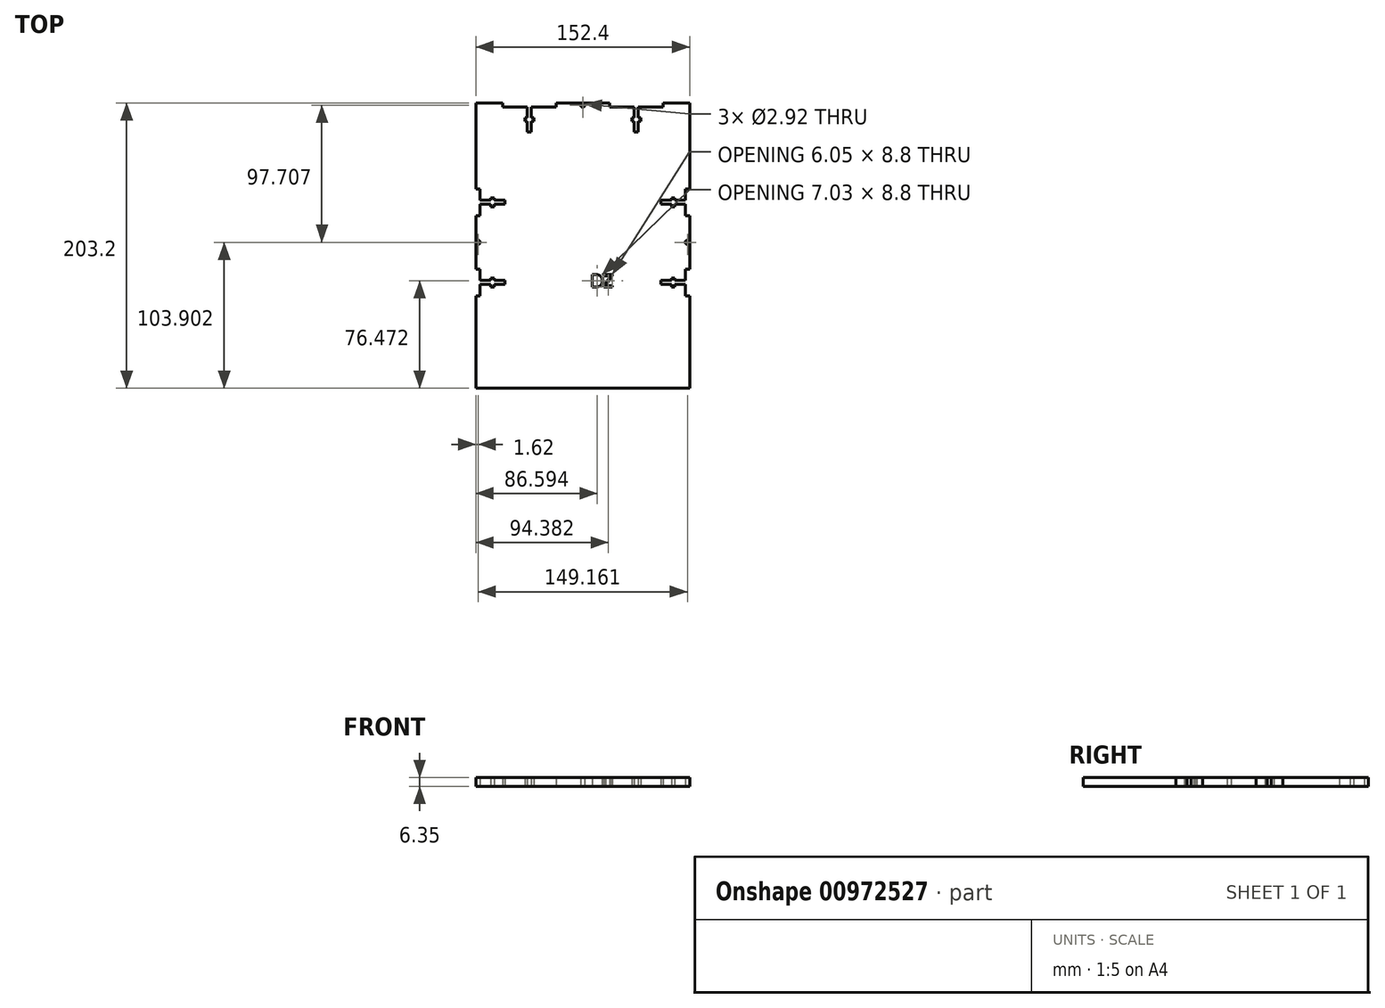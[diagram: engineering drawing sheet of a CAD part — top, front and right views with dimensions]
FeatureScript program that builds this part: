
annotation { "Feature Type Name" : "Feature", "Feature Type Description" : "" }
export const myFeature = defineFeature(function(context is Context, id is Id, definition is map)
    precondition{}
    {
        {
            var Q0;
            Q0=qCreatedBy(makeId("Top.planeOp"),FACE);
            var sketch = newSketch(context, id + "F0", { "sketchPlane" : qUnion([Q0])});
            skLineSegment(sketch, "E0.bottom", {"start": v(-76.2, 101.6) * mm, "end": v(-57.15, 101.6) * mm});
            skLineSegment(sketch, "E0.top", {"start": v(-76.2, -101.6) * mm, "end": v(76.2, -101.6) * mm});
            skLineSegment(sketch, "E0.left", {"start": v(-76.2, 101.6) * mm, "end": v(-76.2, 40.4) * mm});
            skLineSegment(sketch, "E0.right", {"start": v(76.2, 101.6) * mm, "end": v(76.2, 40.4) * mm});
            skLineSegment(sketch, "E1", {"start": v(0, 13.36) * mm, "end": v(-76.2, 13.36) * mm, "construction": true});
            skLineSegment(sketch, "E2", {"start": v(0, 13.36) * mm, "end": v(76.2, 13.36) * mm, "construction": true});
            skLineSegment(sketch, "E3", {"start": v(-22.28, 0) * mm, "end": v(-22.28, 98.63) * mm, "construction": true});
            skLineSegment(sketch, "E4", {"start": v(-22.28, 0) * mm, "end": v(-22.28, -101.6) * mm, "construction": true});
            skLineSegment(sketch, "E5", {"start": v(0, 101.6) * mm, "end": v(0, 98.55) * mm, "construction": true});
            skCircle(sketch, "E6", {"center": v(0, 100) * mm, "radius": 1.46 * mm});
            skLineSegment(sketch, "E7.top", {"start": v(-19.05, 98.63) * mm, "end": v(-36.64, 98.63) * mm});
            skLineSegment(sketch, "E7.left", {"start": v(-19.05, 101.6) * mm, "end": v(-19.05, 98.63) * mm});
            skLineSegment(sketch, "E7.right", {"start": v(-57.15, 101.6) * mm, "end": v(-57.15, 98.63) * mm});
            skLineSegment(sketch, "E8.top", {"start": v(19.05, 98.63) * mm, "end": v(36.64, 98.63) * mm});
            skLineSegment(sketch, "E8.left", {"start": v(19.05, 101.6) * mm, "end": v(19.05, 98.63) * mm});
            skLineSegment(sketch, "E8.right", {"start": v(57.15, 101.6) * mm, "end": v(57.15, 98.63) * mm});
            skLineSegment(sketch, "E9", {"start": v(-36.64, 98.63) * mm, "end": v(-21.4, 98.63) * mm});
            skLineSegment(sketch, "E10", {"start": v(-36.64, 98.63) * mm, "end": v(-19.05, 98.63) * mm});
            skLineSegment(sketch, "E11", {"start": v(-39.56, 98.63) * mm, "end": v(-39.56, 91) * mm});
            skLineSegment(sketch, "E12", {"start": v(-39.56, 91) * mm, "end": v(-41.28, 91) * mm});
            skLineSegment(sketch, "E13", {"start": v(-41.28, 91) * mm, "end": v(-41.28, 88.6) * mm});
            skLineSegment(sketch, "E14", {"start": v(-41.28, 88.6) * mm, "end": v(-39.56, 88.6) * mm});
            skLineSegment(sketch, "E15", {"start": v(-39.56, 88.6) * mm, "end": v(-39.56, 80.98) * mm});
            skLineSegment(sketch, "E16", {"start": v(-38.1, 98.63) * mm, "end": v(-38.1, -9.24) * mm, "construction": true});
            skLineSegment(sketch, "E17", {"start": v(-39.56, 80.98) * mm, "end": v(-38.1, 80.98) * mm});
            skLineSegment(sketch, "E18.MirrorCS", {"start": v(-57.15, 98.63) * mm, "end": v(-39.56, 98.63) * mm});
            skLineSegment(sketch, "E19.MirrorCS", {"start": v(-36.64, 98.63) * mm, "end": v(-36.64, 91) * mm});
            skLineSegment(sketch, "E20.MirrorCS", {"start": v(-36.64, 91) * mm, "end": v(-34.93, 91) * mm});
            skLineSegment(sketch, "E21.MirrorCS", {"start": v(-34.93, 91) * mm, "end": v(-34.93, 88.6) * mm});
            skLineSegment(sketch, "E22.MirrorCS", {"start": v(-34.93, 88.6) * mm, "end": v(-36.64, 88.6) * mm});
            skLineSegment(sketch, "E23.MirrorCS", {"start": v(-36.64, 88.6) * mm, "end": v(-36.64, 80.98) * mm});
            skLineSegment(sketch, "E24.MirrorCS", {"start": v(-36.64, 80.98) * mm, "end": v(-38.1, 80.98) * mm});
            skLineSegment(sketch, "E25.MirrorCS", {"start": v(39.56, 98.63) * mm, "end": v(39.56, 91) * mm});
            skLineSegment(sketch, "E26.MirrorCS", {"start": v(39.56, 91) * mm, "end": v(41.28, 91) * mm});
            skLineSegment(sketch, "E27.MirrorCS", {"start": v(41.28, 91) * mm, "end": v(41.28, 88.6) * mm});
            skLineSegment(sketch, "E28.MirrorCS", {"start": v(41.28, 88.6) * mm, "end": v(39.56, 88.6) * mm});
            skLineSegment(sketch, "E29.MirrorCS", {"start": v(39.56, 88.6) * mm, "end": v(39.56, 80.98) * mm});
            skLineSegment(sketch, "E30.MirrorCS", {"start": v(39.56, 80.98) * mm, "end": v(38.1, 80.98) * mm});
            skLineSegment(sketch, "E31.MirrorCS", {"start": v(36.64, 80.98) * mm, "end": v(38.1, 80.98) * mm});
            skLineSegment(sketch, "E32.MirrorCS", {"start": v(36.64, 88.6) * mm, "end": v(36.64, 80.98) * mm});
            skLineSegment(sketch, "E33.MirrorCS", {"start": v(34.93, 88.6) * mm, "end": v(36.64, 88.6) * mm});
            skLineSegment(sketch, "E34.MirrorCS", {"start": v(34.93, 91) * mm, "end": v(34.93, 88.6) * mm});
            skLineSegment(sketch, "E35.MirrorCS", {"start": v(36.64, 91) * mm, "end": v(34.93, 91) * mm});
            skLineSegment(sketch, "E36.MirrorCS", {"start": v(36.64, 98.63) * mm, "end": v(36.64, 91) * mm});
            skLineSegment(sketch, "E37", {"start": v(-76.2, 2.3) * mm, "end": v(-28.83, 2.3) * mm, "construction": true});
            skCircle(sketch, "E38", {"center": v(-74.58, 2.3) * mm, "radius": 1.46 * mm});
            skLineSegment(sketch, "E39.bottom", {"start": v(-76.2, 40.4) * mm, "end": v(-73.23, 40.4) * mm});
            skLineSegment(sketch, "E39.top", {"start": v(-76.2, 21.35) * mm, "end": v(-73.23, 21.35) * mm});
            skLineSegment(sketch, "E39.right", {"start": v(-73.23, 40.4) * mm, "end": v(-73.23, 32.34) * mm});
            skLineSegment(sketch, "E40.bottom", {"start": v(-76.2, -16.75) * mm, "end": v(-73.23, -16.75) * mm});
            skLineSegment(sketch, "E40.top", {"start": v(-76.2, -35.8) * mm, "end": v(-73.23, -35.8) * mm});
            skLineSegment(sketch, "E40.right", {"start": v(-73.23, -16.75) * mm, "end": v(-73.23, -24.81) * mm});
            skLineSegment(sketch, "E41", {"start": v(-74.71, 21.35) * mm, "end": v(-74.71, 2.3) * mm, "construction": true});
            skLineSegment(sketch, "E42", {"start": v(-74.71, 2.3) * mm, "end": v(-74.71, -16.75) * mm, "construction": true});
            skLineSegment(sketch, "E43", {"start": v(-73.23, 32.34) * mm, "end": v(-65.6, 32.34) * mm});
            skLineSegment(sketch, "E44", {"start": v(-65.6, 32.34) * mm, "end": v(-65.6, 34.05) * mm});
            skLineSegment(sketch, "E45", {"start": v(-65.6, 34.05) * mm, "end": v(-63.2, 34.05) * mm});
            skLineSegment(sketch, "E46", {"start": v(-63.2, 34.05) * mm, "end": v(-63.2, 32.34) * mm});
            skLineSegment(sketch, "E47", {"start": v(-63.2, 32.34) * mm, "end": v(-55.58, 32.34) * mm});
            skLineSegment(sketch, "E48", {"start": v(-55.58, 32.34) * mm, "end": v(-55.58, 30.88) * mm});
            skLineSegment(sketch, "E49", {"start": v(-36.64, 91) * mm, "end": v(-38.1, 91) * mm, "construction": true});
            skLineSegment(sketch, "E50", {"start": v(-69.93, 30.88) * mm, "end": v(-69.93, 30.6) * mm, "construction": true});
            skLineSegment(sketch, "E51", {"start": v(-55.58, 30.88) * mm, "end": v(-73.23, 30.88) * mm, "construction": true});
            skLineSegment(sketch, "E52.MirrorCS", {"start": v(-73.23, 29.42) * mm, "end": v(-65.6, 29.42) * mm});
            skLineSegment(sketch, "E53.MirrorCS", {"start": v(-65.6, 29.42) * mm, "end": v(-65.6, 27.7) * mm});
            skLineSegment(sketch, "E54.MirrorCS", {"start": v(-65.6, 27.7) * mm, "end": v(-63.2, 27.7) * mm});
            skLineSegment(sketch, "E55.MirrorCS", {"start": v(-63.2, 27.7) * mm, "end": v(-63.2, 29.42) * mm});
            skLineSegment(sketch, "E56.MirrorCS", {"start": v(-63.2, 29.42) * mm, "end": v(-55.58, 29.42) * mm});
            skLineSegment(sketch, "E57.MirrorCS", {"start": v(-55.58, 29.42) * mm, "end": v(-55.58, 30.88) * mm});
            skLineSegment(sketch, "E58.MirrorCS", {"start": v(-73.23, -27.73) * mm, "end": v(-65.6, -27.73) * mm});
            skLineSegment(sketch, "E59.MirrorCS", {"start": v(-73.23, -24.81) * mm, "end": v(-65.6, -24.81) * mm});
            skLineSegment(sketch, "E60.MirrorCS", {"start": v(-65.6, -27.73) * mm, "end": v(-65.6, -29.45) * mm});
            skLineSegment(sketch, "E61.MirrorCS", {"start": v(-65.6, -29.45) * mm, "end": v(-63.2, -29.45) * mm});
            skLineSegment(sketch, "E62.MirrorCS", {"start": v(-63.2, -29.45) * mm, "end": v(-63.2, -27.73) * mm});
            skLineSegment(sketch, "E63.MirrorCS", {"start": v(-63.2, -27.73) * mm, "end": v(-55.58, -27.73) * mm});
            skLineSegment(sketch, "E64.MirrorCS", {"start": v(-55.58, -24.81) * mm, "end": v(-55.58, -26.27) * mm});
            skLineSegment(sketch, "E65.MirrorCS", {"start": v(-63.2, -24.81) * mm, "end": v(-55.58, -24.81) * mm});
            skLineSegment(sketch, "E66.MirrorCS", {"start": v(-63.2, -23.1) * mm, "end": v(-63.2, -24.81) * mm});
            skLineSegment(sketch, "E67.MirrorCS", {"start": v(-65.6, -23.1) * mm, "end": v(-63.2, -23.1) * mm});
            skLineSegment(sketch, "E68.MirrorCS", {"start": v(-65.6, -24.81) * mm, "end": v(-65.6, -23.1) * mm});
            skLineSegment(sketch, "E69", {"start": v(-55.58, -26.27) * mm, "end": v(-55.58, -27.73) * mm});
            skLineSegment(sketch, "E70.MirrorCS", {"start": v(73.23, -27.73) * mm, "end": v(65.6, -27.73) * mm});
            skLineSegment(sketch, "E71.MirrorCS", {"start": v(73.23, -16.75) * mm, "end": v(73.23, -24.81) * mm});
            skLineSegment(sketch, "E72.MirrorCS", {"start": v(76.2, -16.75) * mm, "end": v(73.23, -16.75) * mm});
            skLineSegment(sketch, "E73.MirrorCS", {"start": v(76.2, -35.8) * mm, "end": v(73.23, -35.8) * mm});
            skLineSegment(sketch, "E74.MirrorCS", {"start": v(76.2, 21.35) * mm, "end": v(73.23, 21.35) * mm});
            skLineSegment(sketch, "E75.MirrorCS", {"start": v(73.23, 40.4) * mm, "end": v(73.23, 32.34) * mm});
            skLineSegment(sketch, "E76.MirrorCS", {"start": v(76.2, 40.4) * mm, "end": v(73.23, 40.4) * mm});
            skLineSegment(sketch, "E77.MirrorCS", {"start": v(73.23, 29.42) * mm, "end": v(65.6, 29.42) * mm});
            skLineSegment(sketch, "E78.MirrorCS", {"start": v(65.6, 29.42) * mm, "end": v(65.6, 27.7) * mm});
            skLineSegment(sketch, "E79.MirrorCS", {"start": v(65.6, 27.7) * mm, "end": v(63.2, 27.7) * mm});
            skLineSegment(sketch, "E80.MirrorCS", {"start": v(63.2, 27.7) * mm, "end": v(63.2, 29.42) * mm});
            skLineSegment(sketch, "E81.MirrorCS", {"start": v(63.2, 29.42) * mm, "end": v(55.58, 29.42) * mm});
            skLineSegment(sketch, "E82.MirrorCS", {"start": v(55.58, 29.42) * mm, "end": v(55.58, 30.88) * mm});
            skLineSegment(sketch, "E83.MirrorCS", {"start": v(63.2, 32.34) * mm, "end": v(55.58, 32.34) * mm});
            skLineSegment(sketch, "E84.MirrorCS", {"start": v(63.2, 34.05) * mm, "end": v(63.2, 32.34) * mm});
            skLineSegment(sketch, "E85.MirrorCS", {"start": v(65.6, 34.05) * mm, "end": v(63.2, 34.05) * mm});
            skLineSegment(sketch, "E86.MirrorCS", {"start": v(65.6, 32.34) * mm, "end": v(65.6, 34.05) * mm});
            skLineSegment(sketch, "E87.MirrorCS", {"start": v(73.23, 32.34) * mm, "end": v(65.6, 32.34) * mm});
            skLineSegment(sketch, "E88.MirrorCS", {"start": v(73.23, -24.81) * mm, "end": v(65.6, -24.81) * mm});
            skLineSegment(sketch, "E89.MirrorCS", {"start": v(65.6, -23.1) * mm, "end": v(63.2, -23.1) * mm});
            skLineSegment(sketch, "E90.MirrorCS", {"start": v(65.6, -24.81) * mm, "end": v(65.6, -23.1) * mm});
            skLineSegment(sketch, "E91.MirrorCS", {"start": v(63.2, -23.1) * mm, "end": v(63.2, -24.81) * mm});
            skLineSegment(sketch, "E92.MirrorCS", {"start": v(63.2, -24.81) * mm, "end": v(55.58, -24.81) * mm});
            skLineSegment(sketch, "E93.MirrorCS", {"start": v(55.58, -24.81) * mm, "end": v(55.58, -26.27) * mm});
            skLineSegment(sketch, "E94.MirrorCS", {"start": v(55.58, -26.27) * mm, "end": v(55.58, -27.73) * mm});
            skLineSegment(sketch, "E95.MirrorCS", {"start": v(63.2, -27.73) * mm, "end": v(55.58, -27.73) * mm});
            skLineSegment(sketch, "E96.MirrorCS", {"start": v(63.2, -29.45) * mm, "end": v(63.2, -27.73) * mm});
            skLineSegment(sketch, "E97.MirrorCS", {"start": v(65.6, -29.45) * mm, "end": v(63.2, -29.45) * mm});
            skLineSegment(sketch, "E98.MirrorCS", {"start": v(65.6, -27.73) * mm, "end": v(65.6, -29.45) * mm});
            skCircle(sketch, "E99.MirrorC", {"center": v(74.58, 2.3) * mm, "radius": 1.46 * mm});
            skLineSegment(sketch, "E100.MirrorCS", {"start": v(55.58, 32.34) * mm, "end": v(55.58, 30.88) * mm});
            skText(sketch, "E101", { "text": "DZ", "fontName": "OpenSans-Regular.ttf"});
            skLineSegment(sketch, "E102.trimOffspring", {"start": v(-76.2, -35.8) * mm, "end": v(-76.2, -101.6) * mm});
            skLineSegment(sketch, "E103.trimOffspring", {"start": v(-73.23, 29.42) * mm, "end": v(-73.23, 21.35) * mm});
            skLineSegment(sketch, "E104.trimOffspring", {"start": v(76.2, 21.35) * mm, "end": v(76.2, -16.75) * mm});
            skLineSegment(sketch, "E105.trimOffspring", {"start": v(73.23, 29.42) * mm, "end": v(73.23, 21.35) * mm});
            skLineSegment(sketch, "E106.trimOffspring", {"start": v(76.2, -35.8) * mm, "end": v(76.2, -101.6) * mm});
            skLineSegment(sketch, "E107.trimOffspring", {"start": v(73.23, -27.73) * mm, "end": v(73.23, -35.8) * mm});
            skLineSegment(sketch, "E108.trimOffspring", {"start": v(-73.23, -27.73) * mm, "end": v(-73.23, -35.8) * mm});
            skLineSegment(sketch, "E109.trimOffspring", {"start": v(57.15, 101.6) * mm, "end": v(76.2, 101.6) * mm});
            skLineSegment(sketch, "E110.trimOffspring", {"start": v(39.56, 98.63) * mm, "end": v(57.15, 98.63) * mm});
            skLineSegment(sketch, "E111.trimOffspring", {"start": v(-19.05, 101.6) * mm, "end": v(19.05, 101.6) * mm});
            skPoint(sketch, "E112.orphan", {"position": v(-38.1, 101.6) * mm});
            skPoint(sketch, "E113.end.orphan", {"position": v(-38.1, 100.11) * mm});
            skPoint(sketch, "E113.start.orphan", {"position": v(-57.15, 100.11) * mm});
            skPoint(sketch, "E114.orphan", {"position": v(-19.05, 100.11) * mm});
            skPoint(sketch, "E115.orphan", {"position": v(19.05, 100.11) * mm});
            skPoint(sketch, "E116.orphan", {"position": v(19.05, 99.53) * mm});
            skPoint(sketch, "E117.orphan", {"position": v(-19.05, 100.5) * mm});
            skLineSegment(sketch, "E118.trimOffspring", {"start": v(-39.56, 98.63) * mm, "end": v(-57.15, 98.63) * mm});
            skLineSegment(sketch, "E119.trimOffspring", {"start": v(-76.2, 21.35) * mm, "end": v(-76.2, -16.75) * mm});
            skLineSegment(sketch, "E120.trimOffspring", {"start": v(0, 13.36) * mm, "end": v(0, -101.6) * mm, "construction": true});
            const initialGuessF0  = {"E101": [0.00567, -0.02953, 1, 0, 0.00888]};
            skSetInitialGuess(sketch, initialGuessF0);
            skSolve(sketch);
        }
        {
            var Q0;
            {var subQ30=sQuery(id+"F0.wireOp",EDGE,"E7.right");Q0=makeQuery(id+"F0.imprint","IMPRINT",FACE,{"disambiguationData":[TD([[makeQuery(id+"F0.imprint","IMPRINT",EDGE,{"derivedFrom":subQ30}),-1.0]])]});}
            var Q1;
            {var subQ17=sQuery(id+"F0.wireOp",EDGE,"E8.right");Q1=makeQuery(id+"F0.imprint","IMPRINT",FACE,{"disambiguationData":[TD([[makeQuery(id+"F0.imprint","IMPRINT",EDGE,{"derivedFrom":subQ17}),1.0]])]});}
            var Q2;
            {var subQ0=sQuery(id+"F0.wireOp",EDGE,"hTRf1EWx-2PV8-g5uP-djJ1-ZeDew6IlH5Hx");Q2=makeQuery(id+"F0.imprint","IMPRINT",FACE,{"disambiguationData":[TD([[makeQuery(id+"F0.imprint","IMPRINT",EDGE,{"derivedFrom":subQ0}),-1.0]])]});}
            var Q3;
            {var subQ5=sQuery(id+"F0.wireOp",EDGE,"hTRf1EWx-2PV8-g5uP-djJ1-ZeDew6IlH5Hx");Q3=makeQuery(id+"F0.imprint","IMPRINT",FACE,{"disambiguationData":[TD([[makeQuery(id+"F0.imprint","IMPRINT",EDGE,{"derivedFrom":subQ5}),1.0]])]});}
            var Q4;
            {var subQ5=sQuery(id+"F0.wireOp",EDGE,"sVwTZwuD-N8g0-0PtF-3Z6G-4zIeE9RCdML5");Q4=makeQuery(id+"F0.imprint","IMPRINT",FACE,{"disambiguationData":[TD([[makeQuery(id+"F0.imprint","IMPRINT",EDGE,{"derivedFrom":subQ5}),-1.0]])]});}
            var Q5;
            {var subQ0=sQuery(id+"F0.wireOp",EDGE,"sVwTZwuD-N8g0-0PtF-3Z6G-4zIeE9RCdML5");Q5=makeQuery(id+"F0.imprint","IMPRINT",FACE,{"disambiguationData":[TD([[makeQuery(id+"F0.imprint","IMPRINT",EDGE,{"derivedFrom":subQ0}),1.0]])]});}
            extrude(context, id + "F1", {"entities" : qUnion([Q0, Q1, Q2, Q3, Q4, Q5]), "depth" : 6.35 * mm, "offsetDistance" : 25.4 * mm});
        }
    });
